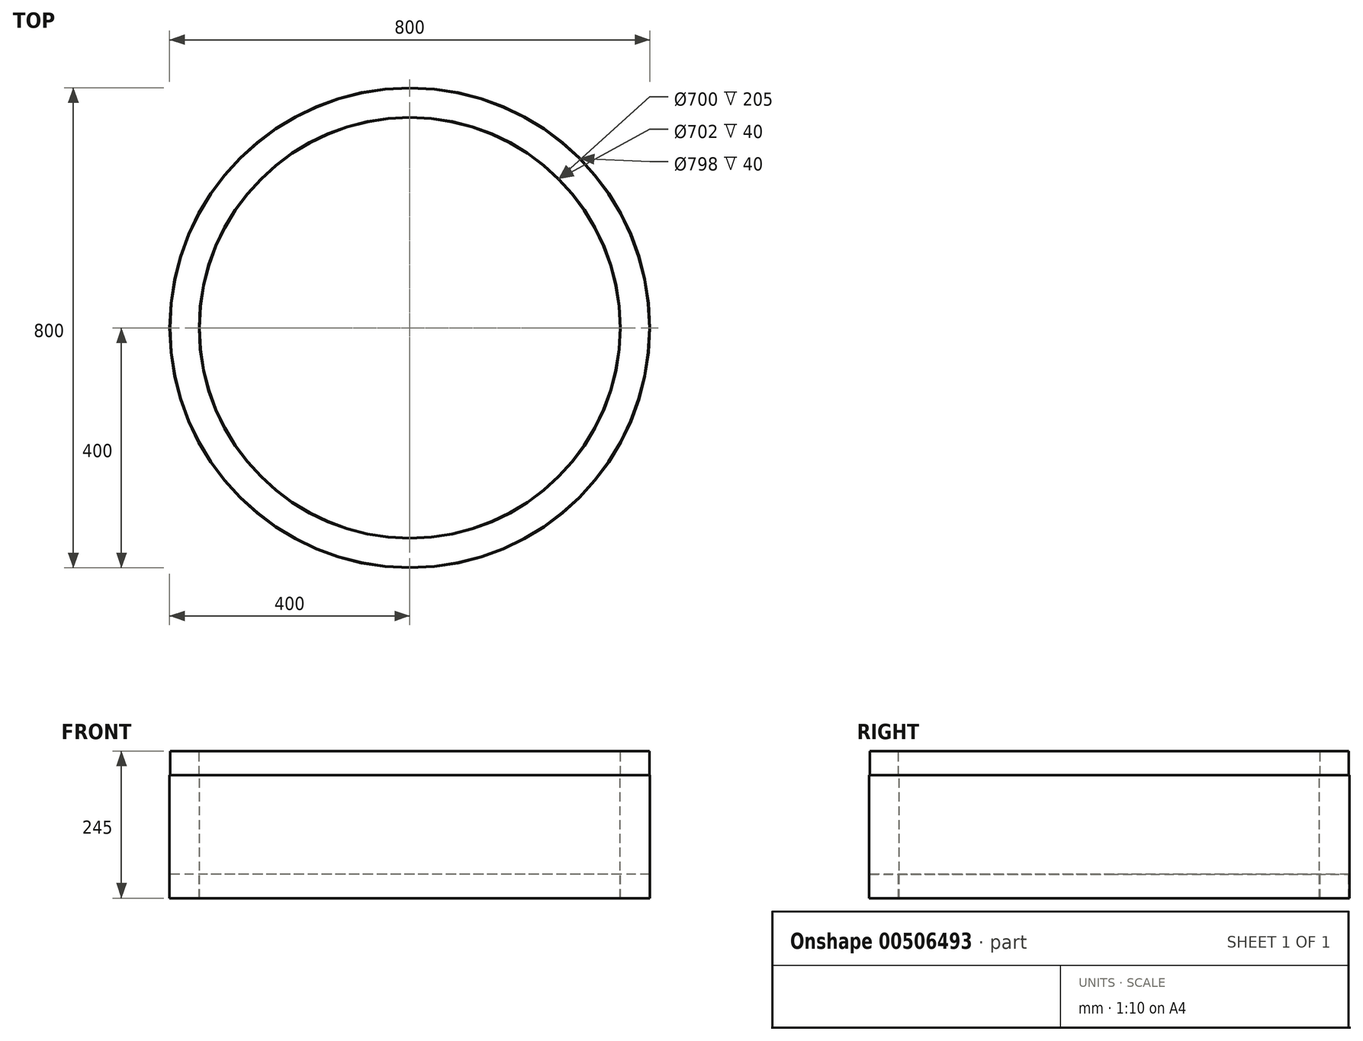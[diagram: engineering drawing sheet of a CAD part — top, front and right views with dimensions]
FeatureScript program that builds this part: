
annotation { "Feature Type Name" : "Feature", "Feature Type Description" : "" }
export const myFeature = defineFeature(function(context is Context, id is Id, definition is map)
    precondition{}
    {
        {
            var Q0;
            Q0=qCreatedBy(makeId("Front.planeOp"),FACE);
            var sketch = newSketch(context, id + "F0", { "sketchPlane" : qUnion([Q0])});
            skLineSegment(sketch, "E0", {"start": v(0, 74.87) * mm, "end": v(0, -73.71) * mm, "construction": true});
            skLineSegment(sketch, "E1", {"start": v(0, 374.84) * mm, "end": v(0, -528.94) * mm, "construction": true});
            skLineSegment(sketch, "E2", {"start": v(-350, -489.75) * mm, "end": v(-350, -284.75) * mm});
            skLineSegment(sketch, "E3", {"start": v(-350, -284.75) * mm, "end": v(-351, -284.75) * mm});
            skLineSegment(sketch, "E4", {"start": v(-351, -284.75) * mm, "end": v(-351, -244.75) * mm});
            skLineSegment(sketch, "E5", {"start": v(-351, -244.75) * mm, "end": v(-399, -244.75) * mm});
            skLineSegment(sketch, "E6", {"start": v(-399, -244.75) * mm, "end": v(-399, -284.75) * mm});
            skLineSegment(sketch, "E7", {"start": v(-399, -284.75) * mm, "end": v(-400, -284.75) * mm});
            skLineSegment(sketch, "E8", {"start": v(-400, -284.75) * mm, "end": v(-400, -489.75) * mm});
            skLineSegment(sketch, "E9", {"start": v(-400, -489.75) * mm, "end": v(-399, -489.75) * mm});
            skLineSegment(sketch, "E10", {"start": v(-399, -489.75) * mm, "end": v(-399, -449.75) * mm});
            skLineSegment(sketch, "E11", {"start": v(-399, -449.75) * mm, "end": v(-351, -449.75) * mm});
            skLineSegment(sketch, "E12", {"start": v(-351, -449.75) * mm, "end": v(-351, -489.75) * mm});
            skLineSegment(sketch, "E13", {"start": v(-351, -489.75) * mm, "end": v(-350, -489.75) * mm});
            skSolve(sketch);
        }
        {
            var Q0;
            Q0=qSketchRegion(id+"F0",true);
            var Q1;
            Q1=sQuery(id+"F0.wireOp",EDGE,"E1");
            revolve(context, id + "F1", {"entities" : qUnion([Q0]), "axis" : qUnion([Q1]), "revolveType" : RevolveType.FULL});
        }
    });
